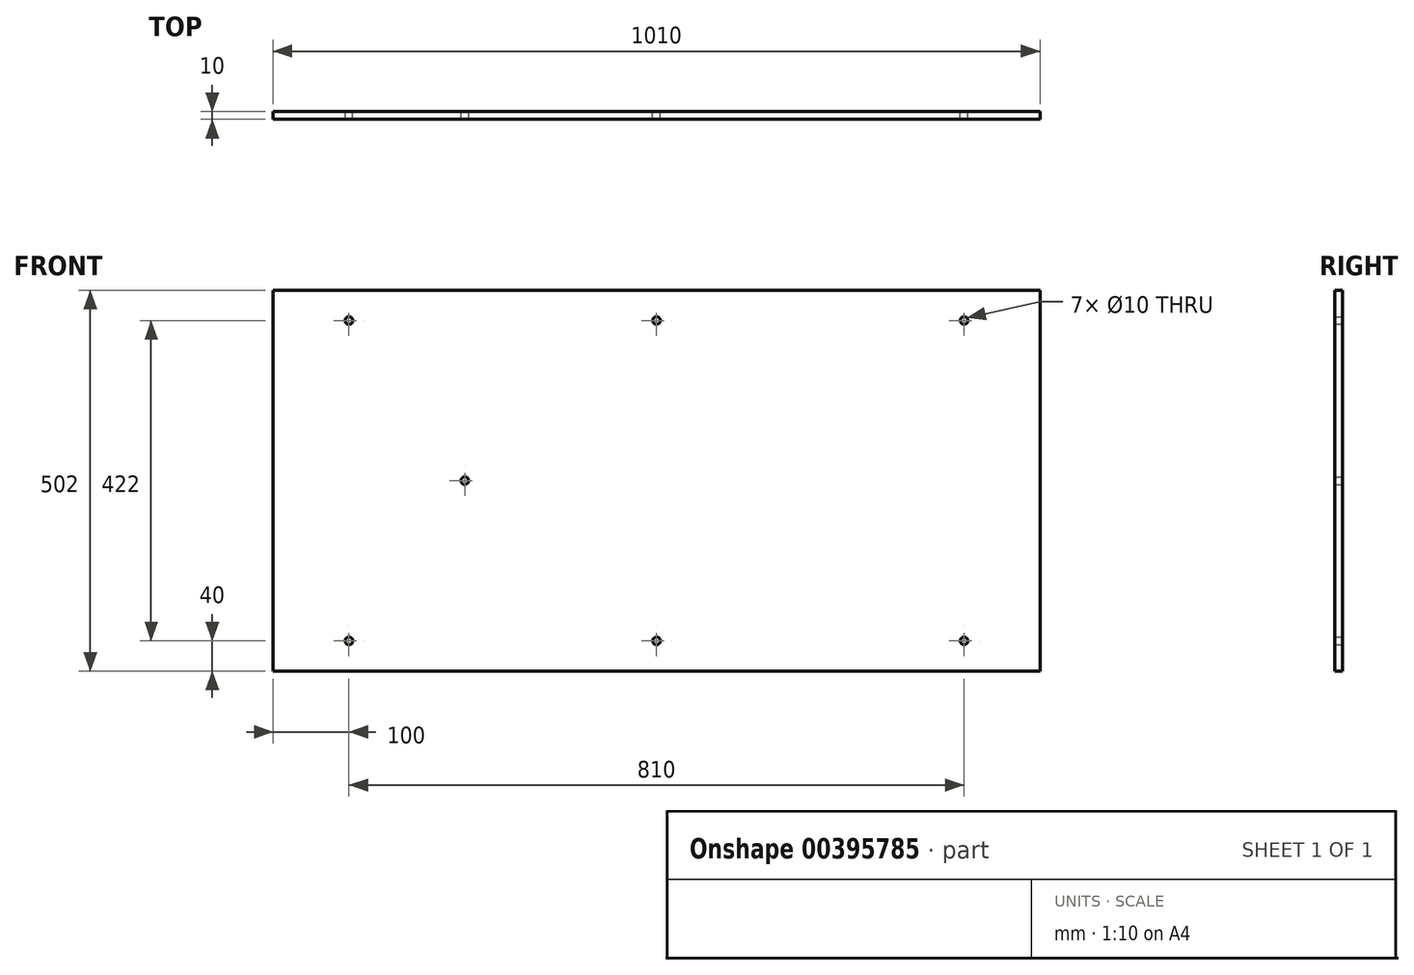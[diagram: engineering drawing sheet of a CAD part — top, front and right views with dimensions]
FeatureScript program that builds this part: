
annotation { "Feature Type Name" : "Feature", "Feature Type Description" : "" }
export const myFeature = defineFeature(function(context is Context, id is Id, definition is map)
    precondition{}
    {
        {
            var Q0;
            Q0=qCreatedBy(makeId("Front.planeOp"),FACE);
            var sketch = newSketch(context, id + "F0", { "sketchPlane" : qUnion([Q0])});
            skLineSegment(sketch, "E0.bottom", {"start": v(0, 0) * mm, "end": v(1010, 0) * mm});
            skLineSegment(sketch, "E0.top", {"start": v(0, 502) * mm, "end": v(1010, 502) * mm});
            skLineSegment(sketch, "E0.left", {"start": v(0, 0) * mm, "end": v(0, 502) * mm});
            skLineSegment(sketch, "E0.right", {"start": v(1010, 0) * mm, "end": v(1010, 502) * mm});
            skLineSegment(sketch, "E1", {"start": v(0, 251) * mm, "end": v(1010, 251) * mm});
            skCircle(sketch, "E2", {"center": v(252.5, 251) * mm, "radius": 5 * mm});
            skLineSegment(sketch, "E3", {"start": v(100, 502) * mm, "end": v(100, 0) * mm});
            skLineSegment(sketch, "E4", {"start": v(910, 502) * mm, "end": v(910, 0) * mm});
            skCircle(sketch, "E5", {"center": v(100, 40) * mm, "radius": 5 * mm});
            skCircle(sketch, "E6", {"center": v(910, 40) * mm, "radius": 5 * mm});
            skCircle(sketch, "E7.MirrorC", {"center": v(100, 462) * mm, "radius": 5 * mm});
            skCircle(sketch, "E8.MirrorC", {"center": v(910, 462) * mm, "radius": 5 * mm});
            skLineSegment(sketch, "E9", {"start": v(505, 502) * mm, "end": v(505, 0) * mm});
            skCircle(sketch, "E10", {"center": v(505, 40) * mm, "radius": 5 * mm});
            skCircle(sketch, "E11.MirrorC", {"center": v(505, 462) * mm, "radius": 5 * mm});
            skSolve(sketch);
        }
        {
            var Q0;
            {var subQ1=sQuery(id+"F0.wireOp",EDGE,"E0.top");Q0=makeQuery(id+"F0.imprint","IMPRINT",FACE,{"disambiguationData":[TD([[makeQuery(id+"F0.imprint","IMPRINT",EDGE,{"derivedFrom":subQ1}),-1.0]])]});}
            var Q1;
            {var subQ6=sQuery(id+"F0.wireOp",EDGE,"E0.bottom");Q1=makeQuery(id+"F0.imprint","IMPRINT",FACE,{"disambiguationData":[TD([[makeQuery(id+"F0.imprint","IMPRINT",EDGE,{"derivedFrom":subQ6}),1.0]])]});}
            var Q2;
            {var subQ6=sQuery(id+"F0.wireOp",EDGE,"E3");var subQ8=sQuery(id+"F0.wireOp",EDGE,"E0.bottom");var subQ9=makeQuery(id+"F0.imprint","INTERSECT",VERTEX,{"derivedFrom":[subQ8,subQ6]});Q2=makeQuery(id+"F0.imprint","IMPRINT",FACE,{"disambiguationData":[TD([[makeQuery(id+"F0.imprint","IMPRINT",EDGE,{"disambiguationData":[TD([[subQ9,-1.0]])],"derivedFrom":subQ8}),1.0]])]});}
            var Q3;
            {var subQ4=sQuery(id+"F0.wireOp",EDGE,"E3");var subQ5=sQuery(id+"F0.wireOp",EDGE,"E0.top");var subQ6=makeQuery(id+"F0.imprint","INTERSECT",VERTEX,{"derivedFrom":[subQ5,subQ4]});Q3=makeQuery(id+"F0.imprint","IMPRINT",FACE,{"disambiguationData":[TD([[makeQuery(id+"F0.imprint","IMPRINT",EDGE,{"disambiguationData":[TD([[subQ6,-1.0]])],"derivedFrom":subQ5}),-1.0]])]});}
            var Q4;
            {var subQ0=sQuery(id+"F0.wireOp",EDGE,"E4");var subQ5=sQuery(id+"F0.wireOp",EDGE,"E0.bottom");var subQ6=makeQuery(id+"F0.imprint","INTERSECT",VERTEX,{"derivedFrom":[subQ5,subQ0]});Q4=makeQuery(id+"F0.imprint","IMPRINT",FACE,{"disambiguationData":[TD([[makeQuery(id+"F0.imprint","IMPRINT",EDGE,{"disambiguationData":[TD([[subQ6,1.0]])],"derivedFrom":subQ5}),1.0]])]});}
            var Q5;
            {var subQ0=sQuery(id+"F0.wireOp",EDGE,"E4");var subQ5=sQuery(id+"F0.wireOp",EDGE,"E0.top");var subQ6=makeQuery(id+"F0.imprint","INTERSECT",VERTEX,{"derivedFrom":[subQ5,subQ0]});Q5=makeQuery(id+"F0.imprint","IMPRINT",FACE,{"disambiguationData":[TD([[makeQuery(id+"F0.imprint","IMPRINT",EDGE,{"disambiguationData":[TD([[subQ6,1.0]])],"derivedFrom":subQ5}),-1.0]])]});}
            extrude(context, id + "F1", {"entities" : qUnion([Q0, Q1, Q2, Q3, Q4, Q5]), "depth" : 10 * mm});
        }
    });
